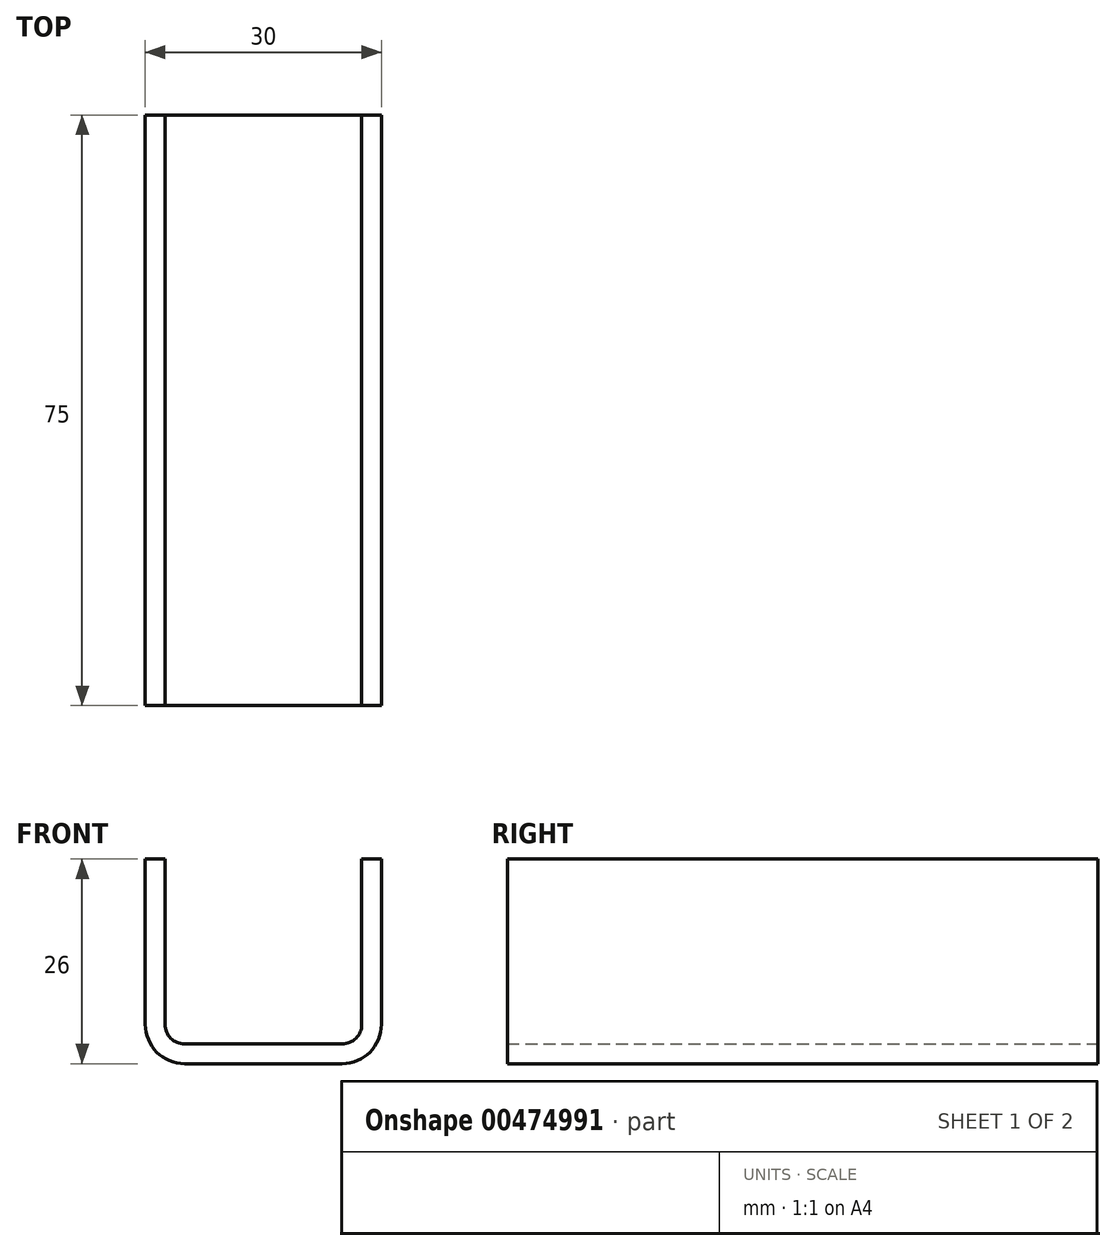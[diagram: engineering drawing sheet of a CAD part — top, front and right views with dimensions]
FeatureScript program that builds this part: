
annotation { "Feature Type Name" : "Feature", "Feature Type Description" : "" }
export const myFeature = defineFeature(function(context is Context, id is Id, definition is map)
    precondition{}
    {
        {
            var Q0;
            Q0=qCreatedBy(makeId("Right.planeOp"),FACE);
            var sketch = newSketch(context, id + "F0", { "sketchPlane" : qUnion([Q0])});
            skLineSegment(sketch, "E0.bottom", {"start": v(-37.5, 13) * mm, "end": v(37.5, 13) * mm});
            skLineSegment(sketch, "E0.top", {"start": v(-37.5, -13) * mm, "end": v(37.5, -13) * mm});
            skLineSegment(sketch, "E0.left", {"start": v(-37.5, 13) * mm, "end": v(-37.5, -13) * mm});
            skLineSegment(sketch, "E0.right", {"start": v(37.5, 13) * mm, "end": v(37.5, -13) * mm});
            skPoint(sketch, "E0.middle", {"position": v(0, 0) * mm});
            skSolve(sketch);
        }
        {
            var Q0;
            Q0=makeQuery(id+"F0.imprint","IMPRINT",FACE,{"disambiguationData":[TD([[makeQuery(id+"F0.imprint","IMPRINT",EDGE,{"derivedFrom":sQuery(id+"F0.wireOp",EDGE,"E0.bottom")}),-1.0]])]});
            extrude(context, id + "F1", {"entities" : qUnion([Q0]), "endBound" : BoundingType.SYMMETRIC, "depth" : 30 * mm});
        }
        {
            var Q0;
            Q0=makeQuery(id+"F1.opExtrude","CAP_EDGE",EDGE,{"disambiguationData":[OSD([sQuery(id+"F0.wireOp",EDGE,"E0.top")])],"isStart":false});
            var Q1;
            Q1=makeQuery(id+"F1.opExtrude","CAP_EDGE",EDGE,{"disambiguationData":[OSD([sQuery(id+"F0.wireOp",EDGE,"E0.top")])],"isStart":true});
            fillet(context, id + "F2", {"entities" : qUnion([Q0, Q1]), "radius" : 5 * mm, "tangentPropagation" : true, "allowEdgeOverflow" : false});
        }
        {
            var Q0;
            Q0=makeQuery(id+"F1.opExtrude","SWEPT_FACE",FACE,{"disambiguationData":[OSD([sQuery(id+"F0.wireOp",EDGE,"E0.bottom")])]});
            var Q1;
            Q1=makeQuery(id+"F1.opExtrude","SWEPT_FACE",FACE,{"disambiguationData":[OSD([sQuery(id+"F0.wireOp",EDGE,"E0.left")])]});
            var Q2;
            Q2=makeQuery(id+"F1.opExtrude","SWEPT_FACE",FACE,{"disambiguationData":[OSD([sQuery(id+"F0.wireOp",EDGE,"E0.right")])]});
            shell(context, id + "F3", {"entities" : qUnion([Q0, Q1, Q2]), "thickness" : 2.5 * mm});
        }
    });
